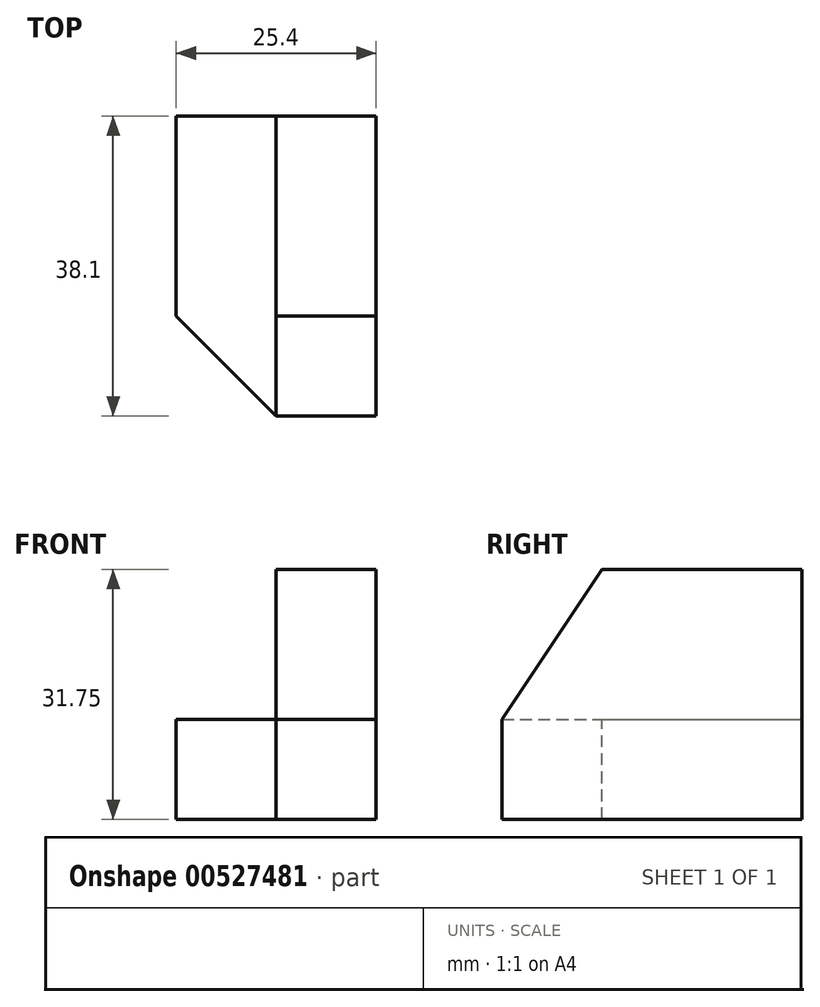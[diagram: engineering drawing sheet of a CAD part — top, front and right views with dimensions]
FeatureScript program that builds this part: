
annotation { "Feature Type Name" : "Feature", "Feature Type Description" : "" }
export const myFeature = defineFeature(function(context is Context, id is Id, definition is map)
    precondition{}
    {
        {
            var Q0;
            Q0=qCreatedBy(makeId("Front.planeOp"),FACE);
            var sketch = newSketch(context, id + "F0", { "sketchPlane" : qUnion([Q0])});
            skLineSegment(sketch, "E0", {"start": v(0, 0) * mm, "end": v(25.4, 0) * mm});
            skLineSegment(sketch, "E1", {"start": v(25.4, 0) * mm, "end": v(25.4, 31.75) * mm});
            skLineSegment(sketch, "E2", {"start": v(25.4, 31.75) * mm, "end": v(12.7, 31.75) * mm});
            skLineSegment(sketch, "E3", {"start": v(0, 0) * mm, "end": v(0, 12.7) * mm});
            skLineSegment(sketch, "E4", {"start": v(12.7, 31.75) * mm, "end": v(12.7, 12.7) * mm});
            skLineSegment(sketch, "E5", {"start": v(0, 12.7) * mm, "end": v(12.7, 12.7) * mm});
            skSolve(sketch);
        }
        {
            var Q0;
            Q0 = qSketchRegion(id + "F0", true);
            extrude(context, id + "F1", {"entities" : qUnion([Q0]), "depth" : 38.1 * mm, "offsetDistance" : 25.4 * mm});
        }
        {
            var Q0;
            Q0=makeQuery(id+"F1.opExtrude","SWEPT_FACE",FACE,{"disambiguationData":[OSD([sQuery(id+"F0.wireOp",EDGE,"E1")])]});
            var sketch = newSketch(context, id + "F2", { "sketchPlane" : qUnion([Q0])});
            skLineSegment(sketch, "E6", {"start": v(-25.4, 31.75) * mm, "end": v(-38.1, 12.7) * mm});
            skSolve(sketch);
        }
        {
            var Q0;
            {var subQ0=sQuery(id+"F2.wireOp",EDGE,"E6");Q0=makeQuery(id+"F2.imprint","IMPRINT",FACE,{"disambiguationData":[TD([[makeQuery(id+"F2.imprint","IMPRINT",EDGE,{"derivedFrom":subQ0}),-1.0]])]});}
            extrude(context, id + "F3", {"entities" : qUnion([Q0]), "operationType" : NewBodyOperationType.REMOVE, "oppositeDirection" : true, "depth" : 25.4 * mm, "offsetDistance" : 25.4 * mm});
        }
        {
            var Q0;
            Q0=makeQuery(id+"F1.opExtrude","SWEPT_FACE",FACE,{"disambiguationData":[OSD([sQuery(id+"F0.wireOp",EDGE,"E5")])]});
            var sketch = newSketch(context, id + "F4", { "sketchPlane" : qUnion([Q0])});
            skLineSegment(sketch, "E7", {"start": v(12.7, -38.1) * mm, "end": v(0, -25.4) * mm});
            skSolve(sketch);
        }
        {
            var Q0;
            {var subQ0=sQuery(id+"F4.wireOp",EDGE,"E7");Q0=makeQuery(id+"F4.imprint","IMPRINT",FACE,{"disambiguationData":[TD([[makeQuery(id+"F4.imprint","IMPRINT",EDGE,{"derivedFrom":subQ0}),1.0]])]});}
            extrude(context, id + "F5", {"entities" : qUnion([Q0]), "operationType" : NewBodyOperationType.REMOVE, "oppositeDirection" : true, "depth" : 25.4 * mm, "offsetDistance" : 25.4 * mm});
        }
    });
